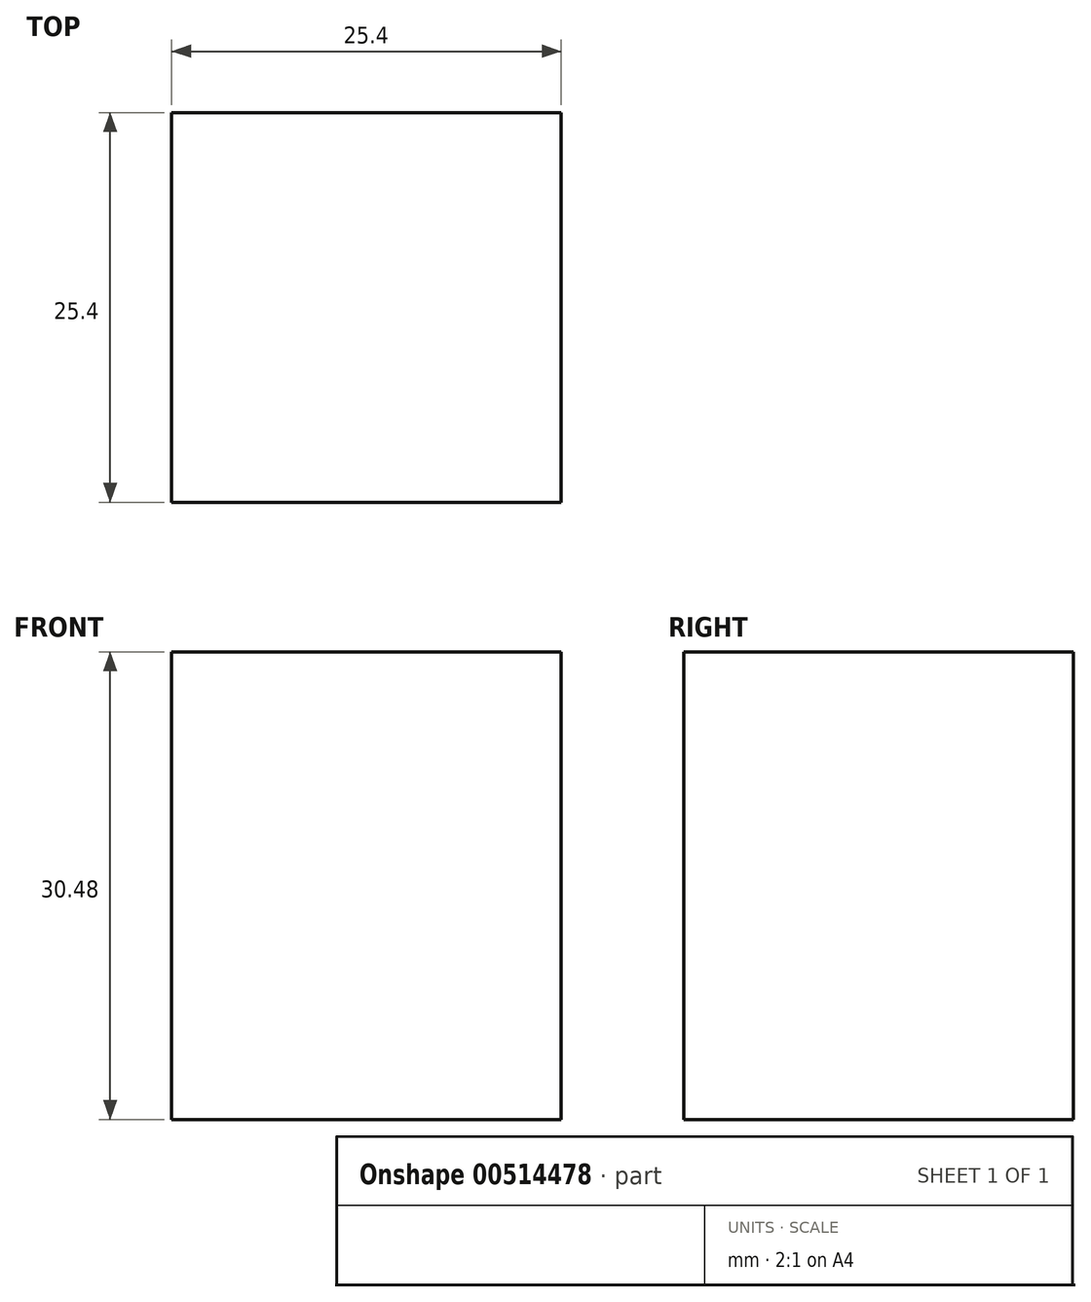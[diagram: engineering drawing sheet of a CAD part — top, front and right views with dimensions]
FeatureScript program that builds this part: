
annotation { "Feature Type Name" : "Feature", "Feature Type Description" : "" }
export const myFeature = defineFeature(function(context is Context, id is Id, definition is map)
    precondition{}
    {
        {
            var Q0;
            Q0=qCreatedBy(makeId("Top.planeOp"),FACE);
            var sketch = newSketch(context, id + "F0", { "sketchPlane" : qUnion([Q0])});
            skLineSegment(sketch, "E0.bottom", {"start": v(0, 0) * mm, "end": v(25.4, 0) * mm});
            skLineSegment(sketch, "E0.top", {"start": v(0, 25.4) * mm, "end": v(25.4, 25.4) * mm});
            skLineSegment(sketch, "E0.left", {"start": v(0, 0) * mm, "end": v(0, 25.4) * mm});
            skLineSegment(sketch, "E0.right", {"start": v(25.4, 0) * mm, "end": v(25.4, 25.4) * mm});
            skSolve(sketch);
        }
        {
            var Q0;
            Q0=makeQuery(id+"F0.imprint","IMPRINT",FACE,{"disambiguationData":[TD([[makeQuery(id+"F0.imprint","IMPRINT",EDGE,{"derivedFrom":sQuery(id+"F0.wireOp",EDGE,"E0.bottom")}),1.0]])]});
            extrude(context, id + "F1", {"entities" : qUnion([Q0]), "depth" : 30.48 * mm, "offsetDistance" : 25.4 * mm});
        }
    });
